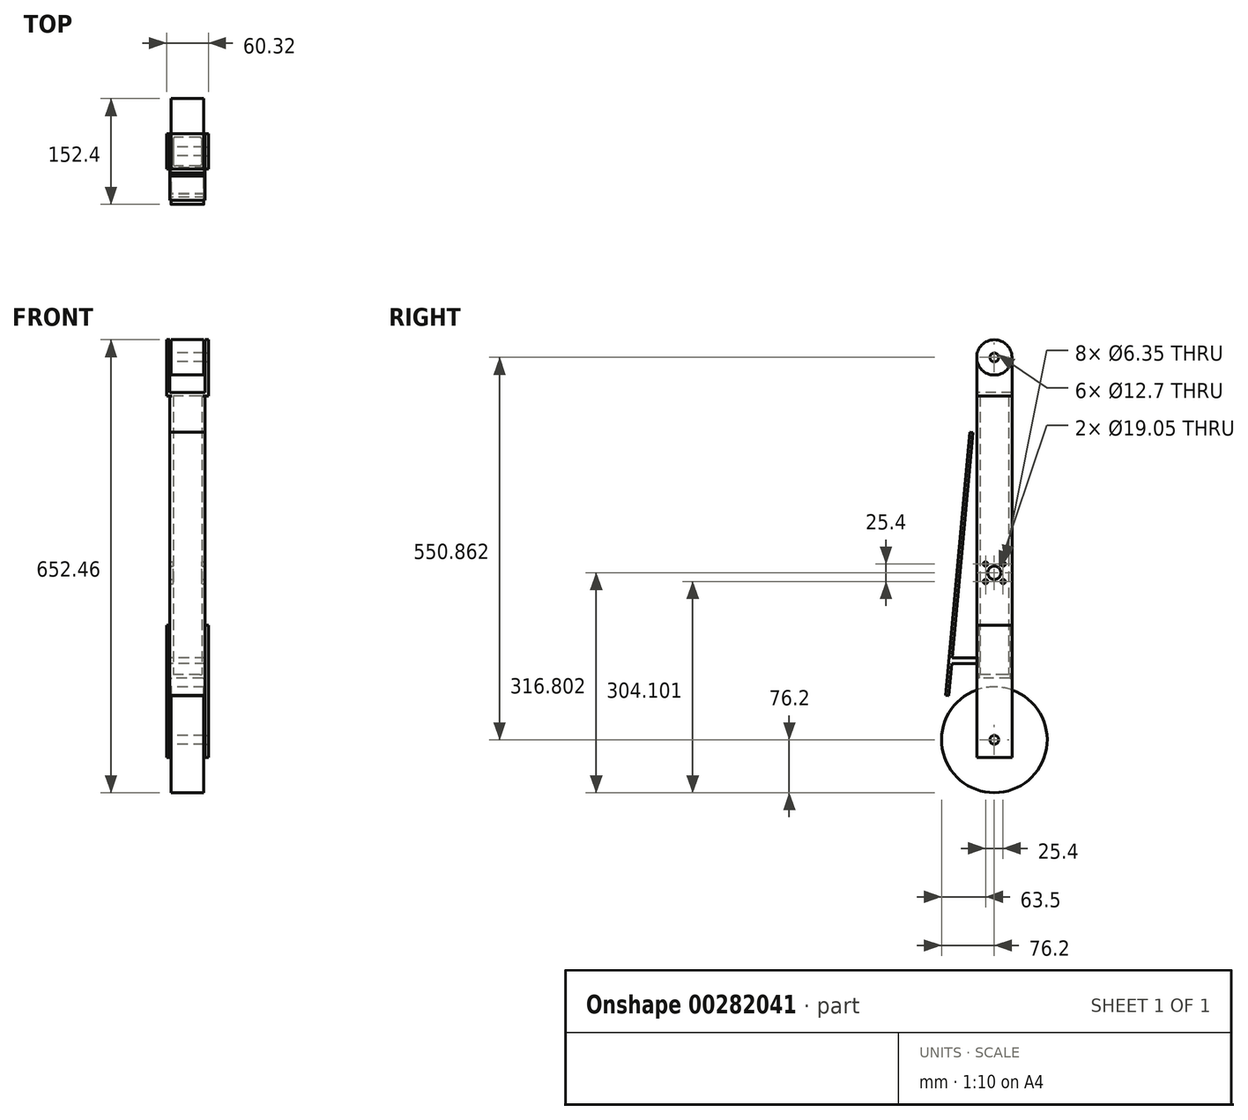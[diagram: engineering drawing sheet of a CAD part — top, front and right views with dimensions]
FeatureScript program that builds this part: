
annotation { "Feature Type Name" : "Feature", "Feature Type Description" : "" }
export const myFeature = defineFeature(function(context is Context, id is Id, definition is map)
    precondition{}
    {
        {
            var Q0;
            Q0=qCreatedBy(makeId("Top.planeOp"),FACE);
            var sketch = newSketch(context, id + "F0", { "sketchPlane" : qUnion([Q0])});
            skLineSegment(sketch, "E0.bottom", {"start": v(17.46, 20.64) * mm, "end": v(-17.46, 20.64) * mm});
            skLineSegment(sketch, "E0.top", {"start": v(17.46, -20.64) * mm, "end": v(-17.46, -20.64) * mm});
            skLineSegment(sketch, "E0.left", {"start": v(20.64, 17.46) * mm, "end": v(20.64, -17.46) * mm});
            skLineSegment(sketch, "E0.right", {"start": v(-20.64, 17.46) * mm, "end": v(-20.64, -17.46) * mm});
            skPoint(sketch, "E0.middle", {"position": v(0, 0) * mm});
            skLineSegment(sketch, "E1.bottom", {"start": v(22.23, 25.4) * mm, "end": v(-22.23, 25.4) * mm});
            skLineSegment(sketch, "E1.top", {"start": v(22.23, -25.4) * mm, "end": v(-22.23, -25.4) * mm});
            skLineSegment(sketch, "E1.left", {"start": v(25.4, 22.23) * mm, "end": v(25.4, -22.23) * mm});
            skLineSegment(sketch, "E1.right", {"start": v(-25.4, 22.23) * mm, "end": v(-25.4, -22.23) * mm});
            skPoint(sketch, "E2.visualSharp", {"position": v(-25.4, 25.4) * mm});
            skArc(sketch, "E2.filletArc", {"start": v(-22.23, 25.4) * mm, "mid": v(-24.47, 24.47) * mm, "end": v(-25.4, 22.23) * mm});
            skPoint(sketch, "E3.visualSharp", {"position": v(-20.64, 20.64) * mm});
            skArc(sketch, "E3.filletArc", {"start": v(-17.46, 20.64) * mm, "mid": v(-19.7, 19.7) * mm, "end": v(-20.64, 17.46) * mm});
            skPoint(sketch, "E4.visualSharp", {"position": v(-20.64, -20.64) * mm});
            skArc(sketch, "E4.filletArc", {"start": v(-20.64, -17.46) * mm, "mid": v(-19.7, -19.7) * mm, "end": v(-17.46, -20.64) * mm});
            skPoint(sketch, "E5.visualSharp", {"position": v(20.64, 20.64) * mm});
            skArc(sketch, "E5.filletArc", {"start": v(20.64, 17.46) * mm, "mid": v(19.7, 19.7) * mm, "end": v(17.46, 20.64) * mm});
            skPoint(sketch, "E6.visualSharp", {"position": v(20.64, -20.64) * mm});
            skArc(sketch, "E6.filletArc", {"start": v(17.46, -20.64) * mm, "mid": v(19.7, -19.7) * mm, "end": v(20.64, -17.46) * mm});
            skPoint(sketch, "E7.visualSharp", {"position": v(-25.4, -25.4) * mm});
            skArc(sketch, "E7.filletArc", {"start": v(-25.4, -22.23) * mm, "mid": v(-24.47, -24.47) * mm, "end": v(-22.23, -25.4) * mm});
            skPoint(sketch, "E8.visualSharp", {"position": v(25.4, -25.4) * mm});
            skArc(sketch, "E8.filletArc", {"start": v(22.23, -25.4) * mm, "mid": v(24.47, -24.47) * mm, "end": v(25.4, -22.23) * mm});
            skPoint(sketch, "E9.visualSharp", {"position": v(25.4, 25.4) * mm});
            skArc(sketch, "E9.filletArc", {"start": v(25.4, 22.23) * mm, "mid": v(24.47, 24.47) * mm, "end": v(22.23, 25.4) * mm});
            skSolve(sketch);
        }
        {
            var Q0;
            Q0 = qSketchRegion(id + "F0", true);
            extrude(context, id + "F1", {"entities" : qUnion([Q0]), "depth" : 406.4 * mm});
        }
        {
            var Q0;
            Q0=makeQuery(id+"F1.opExtrude","CAP_FACE",FACE,{"disambiguationData":[OSD([sQuery(id+"F0.wireOp",EDGE,"E0.bottom"),sQuery(id+"F0.wireOp",EDGE,"E0.top"),sQuery(id+"F0.wireOp",EDGE,"E0.left"),sQuery(id+"F0.wireOp",EDGE,"E0.right"),sQuery(id+"F0.wireOp",EDGE,"E1.bottom"),sQuery(id+"F0.wireOp",EDGE,"E1.top"),sQuery(id+"F0.wireOp",EDGE,"E1.left"),sQuery(id+"F0.wireOp",EDGE,"E1.right"),sQuery(id+"F0.wireOp",EDGE,"E2.filletArc"),sQuery(id+"F0.wireOp",EDGE,"E3.filletArc"),sQuery(id+"F0.wireOp",EDGE,"E4.filletArc"),sQuery(id+"F0.wireOp",EDGE,"E5.filletArc"),sQuery(id+"F0.wireOp",EDGE,"E6.filletArc"),sQuery(id+"F0.wireOp",EDGE,"E7.filletArc"),sQuery(id+"F0.wireOp",EDGE,"E8.filletArc"),sQuery(id+"F0.wireOp",EDGE,"E9.filletArc")])],"isStart":false});
            var sketch = newSketch(context, id + "F2", { "sketchPlane" : qUnion([Q0])});
            skLineSegment(sketch, "E10.bottom", {"start": v(30.16, 25.4) * mm, "end": v(-30.16, 25.4) * mm});
            skLineSegment(sketch, "E10.top", {"start": v(30.16, -25.4) * mm, "end": v(-30.16, -25.4) * mm});
            skLineSegment(sketch, "E10.left", {"start": v(30.16, 25.4) * mm, "end": v(30.16, -25.4) * mm});
            skLineSegment(sketch, "E10.right", {"start": v(-30.16, 25.4) * mm, "end": v(-30.16, -25.4) * mm});
            skPoint(sketch, "E10.middle", {"position": v(0, 0) * mm});
            skSolve(sketch);
        }
        {
            var Q0;
            Q0 = qSketchRegion(id + "F2", true);
            extrude(context, id + "F3", {"entities" : qUnion([Q0]), "operationType" : NewBodyOperationType.ADD, "depth" : 4.76 * mm});
        }
        {
            var Q0;
            Q0=makeQuery(id+"F3.opExtrude","CAP_FACE",FACE,{"disambiguationData":[OSD([sQuery(id+"F2.wireOp",EDGE,"E10.bottom"),sQuery(id+"F2.wireOp",EDGE,"E10.top"),sQuery(id+"F2.wireOp",EDGE,"E10.left"),sQuery(id+"F2.wireOp",EDGE,"E10.right")])],"isStart":false});
            var sketch = newSketch(context, id + "F4", { "sketchPlane" : qUnion([Q0])});
            skLineSegment(sketch, "E11.bottom", {"start": v(-30.16, 25.4) * mm, "end": v(-25.4, 25.4) * mm});
            skLineSegment(sketch, "E11.top", {"start": v(-30.16, -25.4) * mm, "end": v(-25.4, -25.4) * mm});
            skLineSegment(sketch, "E11.left", {"start": v(-30.16, 25.4) * mm, "end": v(-30.16, -25.4) * mm});
            skLineSegment(sketch, "E11.right", {"start": v(-25.4, 25.4) * mm, "end": v(-25.4, -25.4) * mm});
            skLineSegment(sketch, "E12.bottom", {"start": v(30.16, 25.4) * mm, "end": v(25.4, 25.4) * mm});
            skLineSegment(sketch, "E12.top", {"start": v(30.16, -25.4) * mm, "end": v(25.4, -25.4) * mm});
            skLineSegment(sketch, "E12.left", {"start": v(30.16, 25.4) * mm, "end": v(30.16, -25.4) * mm});
            skLineSegment(sketch, "E12.right", {"start": v(25.4, 25.4) * mm, "end": v(25.4, -25.4) * mm});
            skSolve(sketch);
        }
        {
            var Q0;
            Q0 = qSketchRegion(id + "F4", true);
            extrude(context, id + "F5", {"entities" : qUnion([Q0]), "operationType" : NewBodyOperationType.ADD, "depth" : 76.2 * mm});
        }
        {
            var Q0;
            Q0=makeQuery(id+"F5.boolean.opBoolean","MERGE",FACE,{"derivedFrom":[makeQuery(id+"F3.opExtrude","SWEPT_FACE",FACE,{"disambiguationData":[OSD([sQuery(id+"F2.wireOp",EDGE,"E10.left")])]}),makeQuery(id+"F5.opExtrude","SWEPT_FACE",FACE,{"disambiguationData":[OSD([sQuery(id+"F4.wireOp",EDGE,"E12.left")])]})]});
            var sketch = newSketch(context, id + "F6", { "sketchPlane" : qUnion([Q0])});
            skCircle(sketch, "E13", {"center": v(0, 461.96) * mm, "radius": 6.35 * mm});
            skSolve(sketch);
        }
        {
            var Q0;
            Q0 = qSketchRegion(id + "F6", true);
            extrude(context, id + "F7", {"entities" : qUnion([Q0]), "operationType" : NewBodyOperationType.REMOVE, "endBound" : BoundingType.THROUGH_ALL, "oppositeDirection" : true, "depth" : 25.4 * mm});
        }
        {
            var Q0;
            Q0=qCreatedBy(makeId("Top.planeOp"),FACE);
            var sketch = newSketch(context, id + "F8", { "sketchPlane" : qUnion([Q0])});
            skLineSegment(sketch, "E14.bottom", {"start": v(22.23, -25.4) * mm, "end": v(-22.23, -25.4) * mm});
            skLineSegment(sketch, "E14.top", {"start": v(22.23, 25.4) * mm, "end": v(-22.23, 25.4) * mm});
            skLineSegment(sketch, "E14.left", {"start": v(25.4, -22.23) * mm, "end": v(25.4, 22.23) * mm});
            skLineSegment(sketch, "E14.right", {"start": v(-25.4, -22.23) * mm, "end": v(-25.4, 22.23) * mm});
            skPoint(sketch, "E14.middle", {"position": v(0, 0) * mm});
            skPoint(sketch, "E15.visualSharp", {"position": v(-25.4, -25.4) * mm});
            skArc(sketch, "E15.filletArc", {"start": v(-25.4, -22.23) * mm, "mid": v(-24.47, -24.47) * mm, "end": v(-22.23, -25.4) * mm});
            skPoint(sketch, "E16.visualSharp", {"position": v(25.4, -25.4) * mm});
            skArc(sketch, "E16.filletArc", {"start": v(22.23, -25.4) * mm, "mid": v(24.47, -24.47) * mm, "end": v(25.4, -22.23) * mm});
            skPoint(sketch, "E17.visualSharp", {"position": v(-25.4, 25.4) * mm});
            skArc(sketch, "E17.filletArc", {"start": v(-22.23, 25.4) * mm, "mid": v(-24.47, 24.47) * mm, "end": v(-25.4, 22.23) * mm});
            skPoint(sketch, "E18.visualSharp", {"position": v(25.4, 25.4) * mm});
            skArc(sketch, "E18.filletArc", {"start": v(25.4, 22.23) * mm, "mid": v(24.47, 24.47) * mm, "end": v(22.23, 25.4) * mm});
            skSolve(sketch);
        }
        {
            var Q0;
            Q0 = qSketchRegion(id + "F8", true);
            extrude(context, id + "F9", {"entities" : qUnion([Q0]), "operationType" : NewBodyOperationType.ADD, "depth" : 4.76 * mm});
        }
        {
            var Q0;
            Q0=makeQuery(id+"F1.opExtrude","SWEPT_FACE",FACE,{"disambiguationData":[OSD([sQuery(id+"F0.wireOp",EDGE,"E1.left")])]});
            var sketch = newSketch(context, id + "F10", { "sketchPlane" : qUnion([Q0])});
            skLineSegment(sketch, "E19.top", {"start": v(25.4, -114.3) * mm, "end": v(-25.4, -114.3) * mm});
            skLineSegment(sketch, "E19.left", {"start": v(25.4, 76.2) * mm, "end": v(25.4, -114.3) * mm});
            skLineSegment(sketch, "E19.right", {"start": v(-25.4, 76.2) * mm, "end": v(-25.4, -114.3) * mm});
            skPoint(sketch, "E19.middle", {"position": v(0, 0) * mm});
            skLineSegment(sketch, "E20", {"start": v(-25.4, 76.2) * mm, "end": v(25.4, 76.2) * mm});
            skSolve(sketch);
        }
        {
            var Q0;
            Q0 = qSketchRegion(id + "F10", true);
            extrude(context, id + "F11", {"entities" : qUnion([Q0]), "operationType" : NewBodyOperationType.ADD, "depth" : 4.76 * mm});
        }
        {
            var Q0;
            Q0=makeQuery(id+"F1.opExtrude","SWEPT_FACE",FACE,{"disambiguationData":[OSD([sQuery(id+"F0.wireOp",EDGE,"E1.right")])]});
            var sketch = newSketch(context, id + "F12", { "sketchPlane" : qUnion([Q0])});
            skLineSegment(sketch, "E21.top", {"start": v(25.4, -114.3) * mm, "end": v(-25.4, -114.3) * mm});
            skLineSegment(sketch, "E21.left", {"start": v(25.4, 76.2) * mm, "end": v(25.4, -114.3) * mm});
            skLineSegment(sketch, "E21.right", {"start": v(-25.4, 76.2) * mm, "end": v(-25.4, -114.3) * mm});
            skPoint(sketch, "E21.middle", {"position": v(0, 0) * mm});
            skLineSegment(sketch, "E22", {"start": v(-25.4, 76.2) * mm, "end": v(25.4, 76.2) * mm});
            skSolve(sketch);
        }
        {
            var Q0;
            Q0 = qSketchRegion(id + "F12", true);
            extrude(context, id + "F13", {"entities" : qUnion([Q0]), "operationType" : NewBodyOperationType.ADD, "depth" : 4.76 * mm});
        }
        {
            var Q0;
            Q0=makeQuery(id+"F11.opExtrude","CAP_FACE",FACE,{"disambiguationData":[OSD([sQuery(id+"F10.wireOp",EDGE,"E19.top"),sQuery(id+"F10.wireOp",EDGE,"E19.left"),sQuery(id+"F10.wireOp",EDGE,"E19.right"),sQuery(id+"F10.wireOp",EDGE,"E20")])],"isStart":false});
            var sketch = newSketch(context, id + "F14", { "sketchPlane" : qUnion([Q0])});
            skCircle(sketch, "E23", {"center": v(0, -88.9) * mm, "radius": 6.35 * mm});
            skSolve(sketch);
        }
        {
            var Q0;
            Q0 = qSketchRegion(id + "F14", true);
            extrude(context, id + "F15", {"entities" : qUnion([Q0]), "operationType" : NewBodyOperationType.REMOVE, "endBound" : BoundingType.THROUGH_ALL, "oppositeDirection" : true, "depth" : 25.4 * mm});
        }
        {
            var Q0;
            Q0=makeQuery(id+"F5.boolean.opBoolean","MERGE",FACE,{"derivedFrom":[makeQuery(id+"F3.opExtrude","SWEPT_FACE",FACE,{"disambiguationData":[OSD([sQuery(id+"F2.wireOp",EDGE,"E10.left")])]}),makeQuery(id+"F5.opExtrude","SWEPT_FACE",FACE,{"disambiguationData":[OSD([sQuery(id+"F4.wireOp",EDGE,"E12.left")])]})]});
            var sketch = newSketch(context, id + "F16", { "sketchPlane" : qUnion([Q0])});
            skLineSegment(sketch, "E24", {"start": v(0, 461.96) * mm, "end": v(-25.4, 461.96) * mm});
            skLineSegment(sketch, "E25", {"start": v(-25.4, 461.96) * mm, "end": v(25.4, 461.96) * mm});
            skArc(sketch, "E26", {"start": v(25.4, 461.96) * mm, "mid": v(0, 487.36) * mm, "end": v(-25.4, 461.96) * mm});
            skSolve(sketch);
        }
        {
            var Q0;
            {var subQ0=sQuery(id+"F16.wireOp",EDGE,"E25");var subQ1=makeQuery(id+"F16.imprint","IMPRINT",VERTEX,{"derivedFrom":subQ0});Q0=makeQuery(id+"F16.imprint","IMPRINT",FACE,{"disambiguationData":[TD([[makeQuery(id+"F16.imprint","IMPRINT",EDGE,{"disambiguationData":[TD([[subQ1,1.0]])],"derivedFrom":subQ0}),1.0]])]});}
            var Q1;
            {var subQ0=sQuery(id+"F16.wireOp",EDGE,"E26");Q1=makeQuery(id+"F16.imprint","IMPRINT",FACE,{"disambiguationData":[TD([[makeQuery(id+"F16.imprint","IMPRINT",EDGE,{"derivedFrom":subQ0}),-1.0]])]});}
            extrude(context, id + "F17", {"entities" : qUnion([Q0, Q1]), "operationType" : NewBodyOperationType.REMOVE, "endBound" : BoundingType.THROUGH_ALL, "oppositeDirection" : true, "depth" : 25.4 * mm});
        }
        {
            var Q0;
            Q0=makeQuery(id+"F5.opExtrude","SWEPT_FACE",FACE,{"disambiguationData":[OSD([sQuery(id+"F4.wireOp",EDGE,"E11.right")])]});
            var sketch = newSketch(context, id + "F18", { "sketchPlane" : qUnion([Q0])});
            skCircle(sketch, "E27", {"center": v(0, 461.96) * mm, "radius": 25.4 * mm});
            skSolve(sketch);
        }
        {
            var Q0;
            {var subQ1=sQuery(id+"F4.wireOp",EDGE,"E11.right");Q0=makeQuery(id+"F18.imprint","IMPRINT",FACE,{"disambiguationData":[TD([[makeQuery(id+"F18.imprint","IMPRINT",EDGE,{"derivedFrom":makeQuery(id+"F7.boolean.opBoolean","INTERSECT",EDGE,{"derivedFrom":[makeQuery(id+"F5.opExtrude","SWEPT_FACE",FACE,{"disambiguationData":[OSD([subQ1])]}),makeQuery(id+"F7.opExtrude","SWEPT_FACE",FACE,{"disambiguationData":[OSD([sQuery(id+"F6.wireOp",EDGE,"E13")])]})]})}),-1.0]])]});}
            extrude(context, id + "F19", {"entities" : qUnion([Q0]), "operationType" : NewBodyOperationType.ADD, "depth" : 49.02 * mm, "hasSecondDirection" : true, "secondDirectionOppositeDirection" : false, "secondDirectionDepth" : 1.59 * mm});
        }
        {
            var Q0;
            Q0=makeQuery(id+"F13.opExtrude","CAP_FACE",FACE,{"disambiguationData":[OSD([sQuery(id+"F12.wireOp",EDGE,"E21.top"),sQuery(id+"F12.wireOp",EDGE,"E21.left"),sQuery(id+"F12.wireOp",EDGE,"E21.right"),sQuery(id+"F12.wireOp",EDGE,"E22")])],"isStart":true});
            var sketch = newSketch(context, id + "F20", { "sketchPlane" : qUnion([Q0])});
            skCircle(sketch, "E28", {"center": v(0, -88.9) * mm, "radius": 76.2 * mm});
            skCircle(sketch, "E29", {"center": v(0, -88.9) * mm, "radius": 6.35 * mm});
            skSolve(sketch);
        }
        {
            var Q0;
            Q0 = qSketchRegion(id + "F20", true);
            extrude(context, id + "F21", {"entities" : qUnion([Q0]), "operationType" : NewBodyOperationType.ADD, "depth" : 49.02 * mm, "hasSecondDirection" : true, "secondDirectionOppositeDirection" : false, "secondDirectionDepth" : 1.59 * mm});
        }
        {
            var Q0;
            Q0=qCreatedBy(makeId("Right.planeOp"),FACE);
            var sketch = newSketch(context, id + "F22", { "sketchPlane" : qUnion([Q0])});
            skLineSegment(sketch, "E30", {"start": v(-76.2, -88.9) * mm, "end": v(-25.4, 461.96) * mm});
            skLineSegment(sketch, "E31", {"start": v(-35.33, 354.26) * mm, "end": v(-30.6, 353.82) * mm});
            skLineSegment(sketch, "E32", {"start": v(-30.6, 353.82) * mm, "end": v(-65.58, -25.57) * mm});
            skLineSegment(sketch, "E33", {"start": v(-65.58, -25.57) * mm, "end": v(-70.32, -25.13) * mm});
            skLineSegment(sketch, "E34", {"start": v(-61.3, 20.87) * mm, "end": v(-23.28, 20.87) * mm});
            skLineSegment(sketch, "E35", {"start": v(-23.28, 20.87) * mm, "end": v(-23.28, 28.9) * mm});
            skLineSegment(sketch, "E36", {"start": v(-23.28, 28.9) * mm, "end": v(-60.55, 28.9) * mm});
            skSolve(sketch);
        }
        {
            var Q0;
            Q0 = qSketchRegion(id + "F22", true);
            extrude(context, id + "F23", {"entities" : qUnion([Q0]), "depth" : 25.4 * mm, "hasSecondDirection" : true, "secondDirectionOppositeDirection" : true, "secondDirectionDepth" : 25.4 * mm});
        }
        {
            var Q0;
            Q0=makeQuery(id+"F1.opExtrude","SWEPT_FACE",FACE,{"disambiguationData":[OSD([sQuery(id+"F0.wireOp",EDGE,"E1.left")])]});
            var sketch = newSketch(context, id + "F24", { "sketchPlane" : qUnion([Q0])});
            skCircle(sketch, "E37", {"center": v(0, 151.7) * mm, "radius": 9.53 * mm});
            skLineSegment(sketch, "E38.bottom", {"start": v(12.7, 164.4) * mm, "end": v(9.53, 164.4) * mm});
            skLineSegment(sketch, "E38.top", {"start": v(12.7, 139) * mm, "end": v(9.53, 139) * mm});
            skLineSegment(sketch, "E38.left", {"start": v(12.7, 164.4) * mm, "end": v(12.7, 161.23) * mm});
            skLineSegment(sketch, "E38.right", {"start": v(-12.7, 164.4) * mm, "end": v(-12.7, 161.23) * mm});
            skCircle(sketch, "E39", {"center": v(-12.7, 164.4) * mm, "radius": 3.18 * mm});
            skCircle(sketch, "E40", {"center": v(12.7, 164.4) * mm, "radius": 3.18 * mm});
            skCircle(sketch, "E41", {"center": v(12.7, 139) * mm, "radius": 3.18 * mm});
            skCircle(sketch, "E42", {"center": v(-12.7, 139) * mm, "radius": 3.18 * mm});
            skLineSegment(sketch, "E43.trimOffspring", {"start": v(-9.53, 164.4) * mm, "end": v(-12.7, 164.4) * mm});
            skLineSegment(sketch, "E44.trimOffspring", {"start": v(-9.52, 139) * mm, "end": v(-12.7, 139) * mm});
            skLineSegment(sketch, "E45.trimOffspring", {"start": v(-12.7, 142.18) * mm, "end": v(-12.7, 139) * mm});
            skLineSegment(sketch, "E46.trimOffspring", {"start": v(12.7, 142.18) * mm, "end": v(12.7, 139) * mm});
            skSolve(sketch);
        }
        {
            var Q0;
            Q0 = qSketchRegion(id + "F24", true);
            extrude(context, id + "F25", {"entities" : qUnion([Q0]), "operationType" : NewBodyOperationType.REMOVE, "endBound" : BoundingType.THROUGH_ALL, "oppositeDirection" : true, "depth" : 25.4 * mm});
        }
    });
